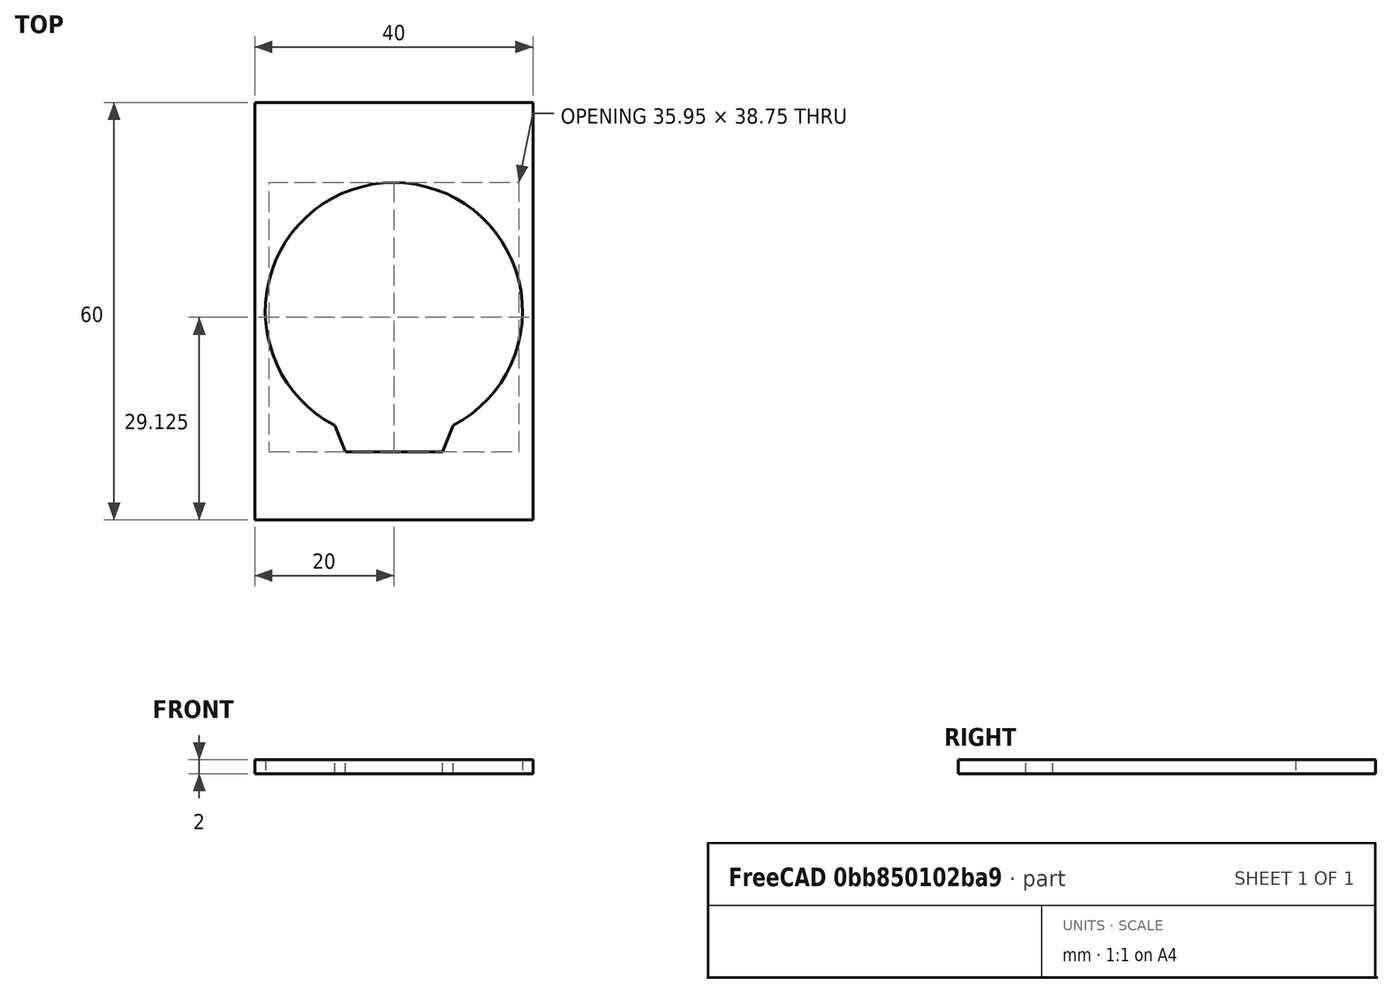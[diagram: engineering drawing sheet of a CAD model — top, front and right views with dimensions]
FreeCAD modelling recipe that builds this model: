
FCSTD DOCUMENT  (FreeCAD 0.20R29177 (Git))
Label: LCD-1.28inch
License: All rights reserved
LicenseURL: http://en.wikipedia.org/wiki/All_rights_reserved
objects: App::DocumentObjectGroup×3, PartDesign::CoordinateSystem×2, Part::FeaturePython×2, App::FeaturePython×1, Sketcher::SketchObject×1, PartDesign::Pad×1, PartDesign::Body×1, App::Link×1, App::Part×1
note: 8 computed .brp shape members not serialized (recipe doc carries the construction recipe); baked Part::Feature solids carry a one-line shape summary decoded from their .brp
EXTERNAL_REF file=LCD-1.28inch-Top.FCStd obj=LCS_Origin
EXTERNAL_REF file=LCD-1.28inch-Top.FCStd obj=Model
EXTERNAL_REF file=../../../.cache/FreeCAD/Cache/FreeCAD_Doc_ca71fdad-f997-481a-a821-e9ea57e04f97_da39a3_40904 obj=LCS_Origin
EXTERNAL_REF file=../../../.cache/FreeCAD/Cache/FreeCAD_Doc_ca71fdad-f997-481a-a821-e9ea57e04f97_da39a3_40904 obj=Assembly
EXTERNAL_REF file=Nut-Holder.FCStd obj=Assembly
EXTERNAL_REF file=../../../.cache/FreeCAD/Cache/FreeCAD_Doc_145d3813-2947-44bf-960b-8cda309f67ea_da39a3_40904 obj=LCS_Origin
EXTERNAL_REF file=../../../.cache/FreeCAD/Cache/FreeCAD_Doc_145d3813-2947-44bf-960b-8cda309f67ea_da39a3_40904 obj=Assembly

FEATURE [App::DocumentObjectGroup] Parts
FEATURE [PartDesign::CoordinateSystem] LCS_Origin
  AttacherType = Attacher::AttachEngine3D
  MapMode = 2
  Support = -> [X_Axis]
FEATURE [App::DocumentObjectGroup] Constraints
FEATURE [App::FeaturePython] Variables  # WARN: FeaturePython — macro-defined, semantics opaque (R4)
  Type = App::PropertyContainer
FEATURE [App::DocumentObjectGroup] Configurations
FEATURE [PartDesign::CoordinateSystem] LCS_0
  AttacherType = Attacher::AttachEngine3D
  MapMode = 2
  Support = -> [X_Axis001]
FEATURE [Sketcher::SketchObject] Sketch
  FullyConstrained = true
  MapMode = 5
  Support = -> [XY_Plane001]
  sketch-geometry (8):
    g0: ArcOfCircle CenterX=0 CenterY=0 CenterZ=0 NormalX=0 NormalY=0 NormalZ=1 AngleXU=0 Radius=18.5 StartAngle=5.18978 EndAngle=10.5182
    g1: LineSegment StartX=-8.5 StartY=-16.4317 StartZ=0 EndX=-7 EndY=-20.25 EndZ=0
    g2: LineSegment StartX=-7 StartY=-20.25 StartZ=0 EndX=7 EndY=-20.25 EndZ=0
    g3: LineSegment StartX=7 StartY=-20.25 StartZ=0 EndX=8.5 EndY=-16.4317 EndZ=0
    g4: LineSegment StartX=-20 StartY=30 StartZ=0 EndX=20 EndY=30 EndZ=0
    g5: LineSegment StartX=20 StartY=30 StartZ=0 EndX=20 EndY=-30 EndZ=0
    g6: LineSegment StartX=20 StartY=-30 StartZ=0 EndX=-20 EndY=-30 EndZ=0
    g7: LineSegment StartX=-20 StartY=-30 StartZ=0 EndX=-20 EndY=30 EndZ=0
  constraints (22):
    c: Coincident(g0,g-1)
    c: Coincident(g1,g0)
    c: Coincident(g2,g1)
    c: Coincident(g3,g2)
    c: Coincident(g3,g0)
    c: DistanceX(g0,g0) = 17
    c: Diameter(g0) = 37
    c: Horizontal(g0,g0)
    c: DistanceX(g2,g2) = 14
    c: Symmetric(g2,g1,g-2)
    c: DistanceY(g2,g0) = 20.25
    c: Coincident(g4,g5)
    c: Coincident(g5,g6)
    c: Coincident(g6,g7)
    c: Coincident(g7,g4)
    c: Horizontal(g4)
    c: Horizontal(g6)
    c: Vertical(g5)
    c: Vertical(g7)
    c: Symmetric(g5,g4,g0)
    c: DistanceY(g7,g7) = 60
    c: DistanceX(g4,g4) = 40
FEATURE [PartDesign::Pad] Pad
  Direction = (0,0,1)
  Length = 2
  Length2 = 10
  Profile = -> Sketch
  ReferenceAxis = -> Sketch [N_Axis]
  Type = 0
FEATURE [PartDesign::Body] Body
  Group = -> [LCS_0,Sketch,Pad]
  Origin = -> Origin001
  Tip = -> Pad
FEATURE [App::Link] LCD_1_28inch_Top
  AttachedBy = #LCS_Origin
  AttachedTo = Parent Assembly#LCS_Origin
  AttachmentOffset = pos=(0,0,6) rot=(0,0,1;0rad)
  LinkPlacement = pos=(0,0,6) rot=(0,0,1;0rad)
  LinkedObject = -> <external LCD-1.28inch-Top.FCStd>#Model
  Placement = pos=(0,0,6) rot=(0,0,1;0rad)
  SolverId = Asm4EE
  expr: Placement = LCS_Origin.Placement * AttachmentOffset * LCD_1_28inch_Top#LCS_Origin.Placement ^ -1
FEATURE [Part::FeaturePython] Nut_Holder_Bottom  # link proxy (typed FeaturePython)
  AttachedBy = #LCS_Origin
  AttachedTo = Parent Assembly#LCS_Origin
  AttachmentOffset = pos=(0,-30,1.2) rot=(0,0,1;0rad)
  LinkedObject = -> <external ../../../.cache/FreeCAD/Cache/FreeCAD_Doc_ca71fdad-f997-481a-a821-e9ea57e04f97_da39a3_40904>#Assembly
  Placement = pos=(0,-30,1.2) rot=(0,0,1;0rad)
  SolverId = Asm4EE
  SourceObject = -> <external Nut-Holder.FCStd>#Assembly
  Type = Asm4::VariantLink
  diameter = 8.6
  height = 4.8
  nut_width = 6
  pocket_height = 4.8
  expr: Placement = LCS_Origin.Placement * AttachmentOffset * varTmpDoc_11#LCS_Origin.Placement ^ -1
FEATURE [Part::FeaturePython] Nut_Holder_Top  # link proxy (typed FeaturePython)
  AttachedBy = #LCS_Origin
  AttachedTo = Parent Assembly#LCS_Origin
  AttachmentOffset = pos=(0,25,1.2) rot=(0,0,1;0rad)
  LinkedObject = -> <external ../../../.cache/FreeCAD/Cache/FreeCAD_Doc_145d3813-2947-44bf-960b-8cda309f67ea_da39a3_40904>#Assembly
  Placement = pos=(0,25,1.2) rot=(0,0,1;0rad)
  SolverId = Asm4EE
  SourceObject = -> <external Nut-Holder.FCStd>#Assembly
  Type = Asm4::VariantLink
  diameter = 8.6
  height = 4.8
  nut_width = 6
  pocket_height = 4.8
  expr: Placement = LCS_Origin.Placement * AttachmentOffset * varTmpDoc_12#LCS_Origin.Placement ^ -1
FEATURE [App::Part] Model
  AssemblyType = Part::Link
  Group = -> [LCS_Origin,Constraints,Variables,Configurations,Body,LCD_1_28inch_Top,Nut_Holder_Bottom,Nut_Holder_Top]
  Origin = -> Origin
  Type = Assembly

RESOLVED EXTERNAL PARTS (link-assembly join: the EXTERNAL_REF files above that resolve inside this repo's crawl, each included once):
---- part LCD-1.28inch-Top.FCStd = doc fcstd_4a86ef362fde ----
FCSTD DOCUMENT  (FreeCAD 0.20R29177 (Git))
Label: LCD-1.28inch-Top
License: All rights reserved
LicenseURL: http://en.wikipedia.org/wiki/All_rights_reserved
objects: App::DocumentObjectGroup×3, PartDesign::CoordinateSystem×2, Sketcher::SketchObject×2, PartDesign::Pad×2, App::FeaturePython×1, PartDesign::Body×1, App::Part×1
note: 9 computed .brp shape members not serialized (recipe doc carries the construction recipe); baked Part::Feature solids carry a one-line shape summary decoded from their .brp

FEATURE [App::DocumentObjectGroup] Parts
FEATURE [PartDesign::CoordinateSystem] LCS_Origin
  AttacherType = Attacher::AttachEngine3D
  MapMode = 2
  Support = -> [X_Axis]
FEATURE [App::DocumentObjectGroup] Constraints
FEATURE [App::FeaturePython] Variables  # WARN: FeaturePython — macro-defined, semantics opaque (R4)
  Type = App::PropertyContainer
FEATURE [App::DocumentObjectGroup] Configurations
FEATURE [PartDesign::CoordinateSystem] LCS_0
  AttacherType = Attacher::AttachEngine3D
  MapMode = 2
  Support = -> [X_Axis001]
FEATURE [Sketcher::SketchObject] Sketch
  FullyConstrained = true
  MapMode = 5
  Support = -> [XY_Plane001]
  sketch-geometry (14):
    g0: ArcOfCircle CenterX=0 CenterY=25 CenterZ=0 NormalX=0 NormalY=0 NormalZ=1 AngleXU=0 Radius=3.5 StartAngle=0 EndAngle=3.14159
    g1: ArcOfCircle CenterX=0 CenterY=-30 CenterZ=0 NormalX=0 NormalY=0 NormalZ=1 AngleXU=0 Radius=3.5 StartAngle=3.14159 EndAngle=6.28319
    g2: LineSegment StartX=-11 StartY=15 StartZ=0 EndX=11 EndY=15 EndZ=0
    g3: LineSegment StartX=11 StartY=15 StartZ=0 EndX=11 EndY=-15 EndZ=0
    g4: LineSegment StartX=11 StartY=-15 StartZ=0 EndX=-11 EndY=-15 EndZ=0
    g5: LineSegment StartX=-11 StartY=-15 StartZ=0 EndX=-11 EndY=15 EndZ=0
    g6: Circle CenterX=0 CenterY=25 CenterZ=0 NormalX=0 NormalY=0 NormalZ=1 AngleXU=0 Radius=1.75
    g7: Circle CenterX=0 CenterY=-30 CenterZ=0 NormalX=0 NormalY=0 NormalZ=1 AngleXU=0 Radius=1.75
    g8: LineSegment StartX=-3.5 StartY=25 StartZ=0 EndX=-17.5 EndY=25 EndZ=0
    g9: LineSegment StartX=-17.5 StartY=25 StartZ=0 EndX=-17.5 EndY=-30 EndZ=0
    g10: LineSegment StartX=-17.5 StartY=-30 StartZ=0 EndX=-3.5 EndY=-30 EndZ=0
    g11: LineSegment StartX=3.5 StartY=-30 StartZ=0 EndX=17.5 EndY=-30 EndZ=0
    g12: LineSegment StartX=17.5 StartY=-30 StartZ=0 EndX=17.5 EndY=25 EndZ=0
    g13: LineSegment StartX=17.5 StartY=25 StartZ=0 EndX=3.5 EndY=25 EndZ=0
  constraints (41):
    c: PointOnObject(g0,g-2)
    c: PointOnObject(g1,g-2)
    c: Coincident(g2,g3)
    c: Coincident(g3,g4)
    c: Coincident(g4,g5)
    c: Coincident(g5,g2)
    c: Horizontal(g2)
    c: Horizontal(g4)
    c: Vertical(g3)
    c: Vertical(g5)
    c: Horizontal(g0,g0)
    c: Coincident(g6,g0)
    c: Diameter(g6) = 3.5
    c: Diameter(g0) = 7
    c: Equal(g0,g1)
    c: Horizontal(g1,g1)
    c: Coincident(g7,g1)
    c: Equal(g7,g6)
    c: DistanceX(g4,g4) = 22
    c: Symmetric(g3,g2,g-1)
    c: DistanceY(g3,g3) = 30
    c: Horizontal(g1,g1)
    c: Coincident(g8,g0)
    c: Horizontal(g8)
    c: Coincident(g9,g8)
    c: Vertical(g9)
    c: Coincident(g10,g9)
    c: Horizontal(g10)
    c: Coincident(g11,g1)
    c: Horizontal(g11)
    c: Coincident(g12,g11)
    c: Vertical(g12)
    c: Coincident(g13,g12)
    c: Coincident(g13,g0)
    c: Horizontal(g13)
    c: Coincident(g10,g1)
    c: DistanceX(g9,g11) = 35
    c: Horizontal(g0,g0)
    c: DistanceY(g-1,g8) = 25
    c: DistanceX(g8,g-1) = 17.5
    c: DistanceY(g9,g-1) = 30
FEATURE [PartDesign::Pad] Pad  label="Plate"
  Direction = (0,0,1)
  Length = 2
  Length2 = 10
  Profile = -> Sketch
  ReferenceAxis = -> Sketch [N_Axis]
  Type = 0
FEATURE [Sketcher::SketchObject] Sketch001
  FullyConstrained = true
  MapMode = 5
  Support = -> [XY_Plane001]
  sketch-geometry (8):
    g0: LineSegment StartX=-15.1 StartY=19.6 StartZ=0 EndX=15.1 EndY=19.6 EndZ=0
    g1: LineSegment StartX=15.1 StartY=19.6 StartZ=0 EndX=15.1 EndY=-19.6 EndZ=0
    g2: LineSegment StartX=15.1 StartY=-19.6 StartZ=0 EndX=-15.1 EndY=-19.6 EndZ=0
    g3: LineSegment StartX=-15.1 StartY=-19.6 StartZ=0 EndX=-15.1 EndY=19.6 EndZ=0
    g4: LineSegment StartX=-13.5 StartY=18 StartZ=0 EndX=13.5 EndY=18 EndZ=0
    g5: LineSegment StartX=13.5 StartY=18 StartZ=0 EndX=13.5 EndY=-18 EndZ=0
    g6: LineSegment StartX=13.5 StartY=-18 StartZ=0 EndX=-13.5 EndY=-18 EndZ=0
    g7: LineSegment StartX=-13.5 StartY=-18 StartZ=0 EndX=-13.5 EndY=18 EndZ=0
  constraints (22):
    c: Coincident(g0,g1)
    c: Coincident(g1,g2)
    c: Coincident(g2,g3)
    c: Coincident(g3,g0)
    c: Horizontal(g0)
    c: Horizontal(g2)
    c: Vertical(g1)
    c: Vertical(g3)
    c: Coincident(g4,g5)
    c: Coincident(g5,g6)
    c: Coincident(g6,g7)
    c: Coincident(g7,g4)
    c: Horizontal(g4)
    c: Horizontal(g6)
    c: Vertical(g5)
    c: Vertical(g7)
    c: Symmetric(g0,g1,g-1)
    c: Symmetric(g4,g5,g-1)
    c: DistanceX(g0,g4) = 1.6
    c: DistanceY(g4,g0) = 1.6
    c: DistanceX(g4,g-1) = 13.5
    c: DistanceY(g6,g-1) = 18
FEATURE [PartDesign::Pad] Pad001  label="Reinforcement"
  BaseFeature = -> Pad
  Direction = (0,0,1)
  Length = 6
  Length2 = 10
  Profile = -> Sketch001
  ReferenceAxis = -> Sketch001 [N_Axis]
  Type = 0
FEATURE [PartDesign::Body] Body
  Group = -> [LCS_0,Sketch,Pad,Sketch001,Pad001]
  Origin = -> Origin001
  Tip = -> Pad001
FEATURE [App::Part] Model
  AssemblyType = Part::Link
  Group = -> [LCS_Origin,Constraints,Variables,Configurations,Body]
  Origin = -> Origin
  Type = Assembly
---- part Nut-Holder.FCStd = doc fcstd_a03749667bbf ----
FCSTD DOCUMENT  (FreeCAD 0.20R29410 (Git))
Label: Nut-Holder
License: All rights reserved
LicenseURL: https://en.wikipedia.org/wiki/All_rights_reserved
objects: App::DocumentObjectGroup×3, PartDesign::CoordinateSystem×3, Sketcher::SketchObject×2, App::FeaturePython×1, PartDesign::Pad×1, PartDesign::Pocket×1, PartDesign::Body×1, App::Part×1
note: 10 computed .brp shape members not serialized (recipe doc carries the construction recipe); baked Part::Feature solids carry a one-line shape summary decoded from their .brp

FEATURE [App::DocumentObjectGroup] Parts
FEATURE [PartDesign::CoordinateSystem] LCS_Origin
  AttacherType = Attacher::AttachEngine3D
  MapMode = 2
  Support = -> [X_Axis]
FEATURE [App::DocumentObjectGroup] Constraints
FEATURE [App::FeaturePython] Variables  # WARN: FeaturePython — macro-defined, semantics opaque (R4)
  Type = App::PropertyContainer
  diameter = 8.6
  height = 9.2
  nut_width = 6
  pocket_height = 4
  expr: diameter = nut_width + 1 + 2 * 0.8
FEATURE [App::DocumentObjectGroup] Configurations
FEATURE [Sketcher::SketchObject] Sketch
  FullyConstrained = true
  MapMode = 5
  expr: Constraints[1] = Variables.diameter
  sketch-geometry (1):
    g0: Circle CenterX=0 CenterY=0 CenterZ=0 NormalX=0 NormalY=0 NormalZ=1 AngleXU=0 Radius=4.3
  constraints (2):
    c: Coincident(g0,g-1)
    c: Diameter(g0) = 8.6
FEATURE [PartDesign::Pad] Pad  label="Enclosure"
  Direction = (0,0,1)
  Length = 9.2
  Length2 = 10
  Profile = -> Sketch
  ReferenceAxis = -> Sketch [N_Axis]
  Refine = true
  Type = 0
  expr: Length = Variables.height
FEATURE [PartDesign::CoordinateSystem] LCS_Origin001
  AttacherType = Attacher::AttachEngine3D
  MapMode = 2
  Support = -> [X_Axis001]
FEATURE [Sketcher::SketchObject] Sketch003
  AttachmentOffset = pos=(0,0,9.2) rot=(0,0,1;0rad)
  FullyConstrained = true
  MapMode = 5
  Placement = pos=(0,0,9.2) rot=(0,0,1;0rad)
  Support = -> [XY_Plane001]
  expr: .AttachmentOffset.Base.z = Variables.height
  expr: Constraints[19] = Variables.nut_width + 1
  sketch-geometry (7):
    g0: LineSegment StartX=-3.5 StartY=0 StartZ=0 EndX=-1.75 EndY=-3.03109 EndZ=0
    g1: LineSegment StartX=-1.75 StartY=-3.03109 StartZ=0 EndX=1.75 EndY=-3.03109 EndZ=0
    g2: LineSegment StartX=1.75 StartY=-3.03109 StartZ=0 EndX=3.5 EndY=0 EndZ=0
    g3: LineSegment StartX=3.5 StartY=0 StartZ=0 EndX=1.75 EndY=3.03109 EndZ=0
    g4: LineSegment StartX=1.75 StartY=3.03109 StartZ=0 EndX=-1.75 EndY=3.03109 EndZ=0
    g5: LineSegment StartX=-1.75 StartY=3.03109 StartZ=0 EndX=-3.5 EndY=0 EndZ=0
    g6: Circle CenterX=0 CenterY=0 CenterZ=0 NormalX=0 NormalY=0 NormalZ=1 AngleXU=0 Radius=3.5
  constraints (16):
    c: Coincident(g0,g1)
    c: Coincident(g1,g2)
    c: Coincident(g2,g3)
    c: Coincident(g3,g4)
    c: Coincident(g4,g5)
    c: Coincident(g5,g0)
    c: Equal(g0, g1-g5) x5
    c: PointOnObject(g0,g6)
    c: PointOnObject(g1,g6)
    c: PointOnObject(g2,g6)
    c: PointOnObject(g3,g6)
    c: PointOnObject(g4,g6)
    c: PointOnObject(g5,g6)
    c: Coincident(g6,g-1)
    c: PointOnObject(g5,g-1)
    c: DistanceX(g0,g2) = 7
FEATURE [PartDesign::Pocket] Pocket  label="Nut Pocket"
  BaseFeature = -> Pad
  Direction = (0,0,-1)
  Length = 4
  Length2 = 5
  Profile = -> Sketch003
  ReferenceAxis = -> Sketch003 [N_Axis]
  Refine = true
  Type = 0
  expr: Length = Variables.pocket_height
FEATURE [PartDesign::Body] Body
  Group = -> [LCS_Origin001,Pad,Sketch,Sketch003,Pocket]
  Origin = -> Origin001
  Tip = -> Pocket
FEATURE [PartDesign::CoordinateSystem] LCS_Top
  AttacherType = Attacher::AttachEngine3D
  MapMode = 45
  Placement = pos=(-1e-16,3e-16,9.2) rot=(0,0,1;0rad)
  Support = -> [Pocket]
FEATURE [App::Part] Assembly
  AssemblyType = Part::Link
  Group = -> [LCS_Origin,Constraints,Variables,Configurations,Body,LCS_Top]
  Origin = -> Origin
  Type = Assembly
